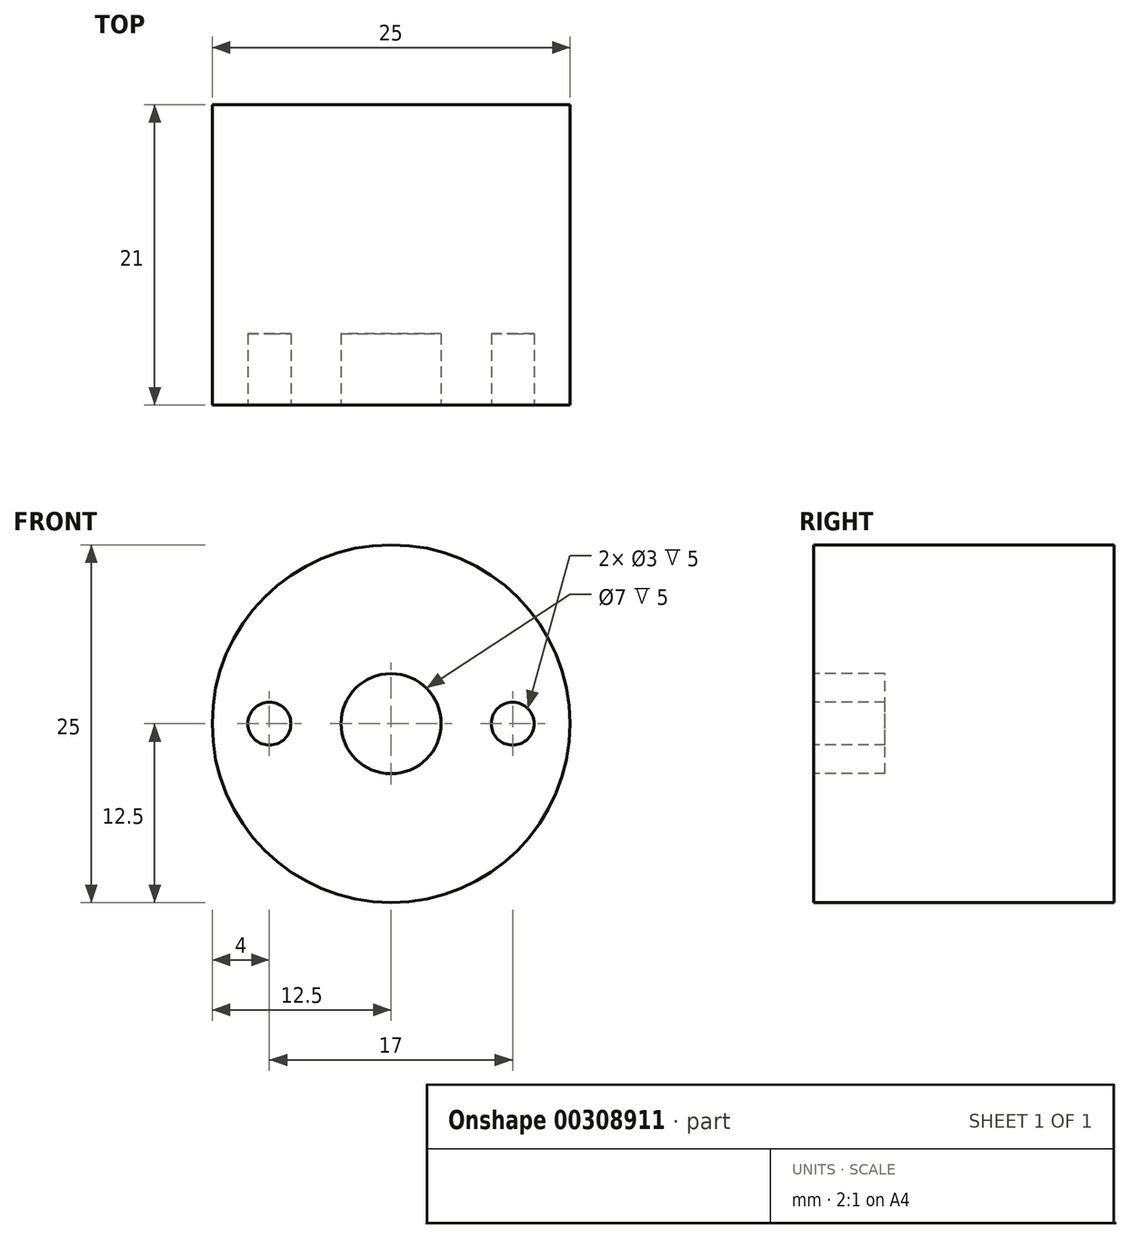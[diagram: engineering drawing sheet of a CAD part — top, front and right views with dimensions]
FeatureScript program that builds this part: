
annotation { "Feature Type Name" : "Feature", "Feature Type Description" : "" }
export const myFeature = defineFeature(function(context is Context, id is Id, definition is map)
    precondition{}
    {
        {
            var Q0;
            Q0=qCreatedBy(makeId("Front.planeOp"),FACE);
            var sketch = newSketch(context, id + "F0", { "sketchPlane" : qUnion([Q0])});
            skCircle(sketch, "E0", {"center": v(0, 0) * mm, "radius": 12.5 * mm});
            skSolve(sketch);
        }
        {
            var Q0;
            Q0 = qSketchRegion(id + "F0", true);
            extrude(context, id + "F1", {"entities" : qUnion([Q0]), "depth" : 21 * mm});
        }
        {
            var Q0;
            Q0=makeQuery(id+"F1.opExtrude","CAP_FACE",FACE,{"disambiguationData":[OSD([sQuery(id+"F0.wireOp",EDGE,"E0")])],"isStart":false});
            var sketch = newSketch(context, id + "F2", { "sketchPlane" : qUnion([Q0])});
            skLineSegment(sketch, "E1", {"start": v(0, 12.5) * mm, "end": v(0, -12.5) * mm, "construction": true});
            skCircle(sketch, "E2", {"center": v(-8.5, 0) * mm, "radius": 1.5 * mm});
            skCircle(sketch, "E3.MirrorC", {"center": v(8.5, 0) * mm, "radius": 1.5 * mm});
            skCircle(sketch, "E4", {"center": v(0, 0) * mm, "radius": 3.5 * mm});
            skSolve(sketch);
        }
        {
            var Q0;
            Q0 = qSketchRegion(id + "F2", true);
            extrude(context, id + "F3", {"entities" : qUnion([Q0]), "operationType" : NewBodyOperationType.REMOVE, "oppositeDirection" : true, "depth" : 5 * mm});
        }
    });
